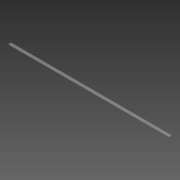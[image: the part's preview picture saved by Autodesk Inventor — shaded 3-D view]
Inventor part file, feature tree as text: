
AUTODESK INVENTOR PART (.ipt)
format: ipt  version: 2013 (Build 170138000, 138)  size: 81,920 bytes
history: native  units: in
note: dims shown in document units (in); Inventor stores cm internally (conversion verified against a paired STEP export)
features: sheet_metal_op x1, sketch x1, other x1
ambient origin geometry x8: Origin, YZ Plane, XZ Plane, XY Plane, X Axis, Y Axis, Z Axis, Center Point
bodies: Solid1 (feature_tree)
feature tree (3):
  sheet_metal_op  "Face1"
  sketch  "Sketch1"  dims[d0=53.0in d1=1.0in d2=0.24in d3=0.12in]
  other  "Plate1"
